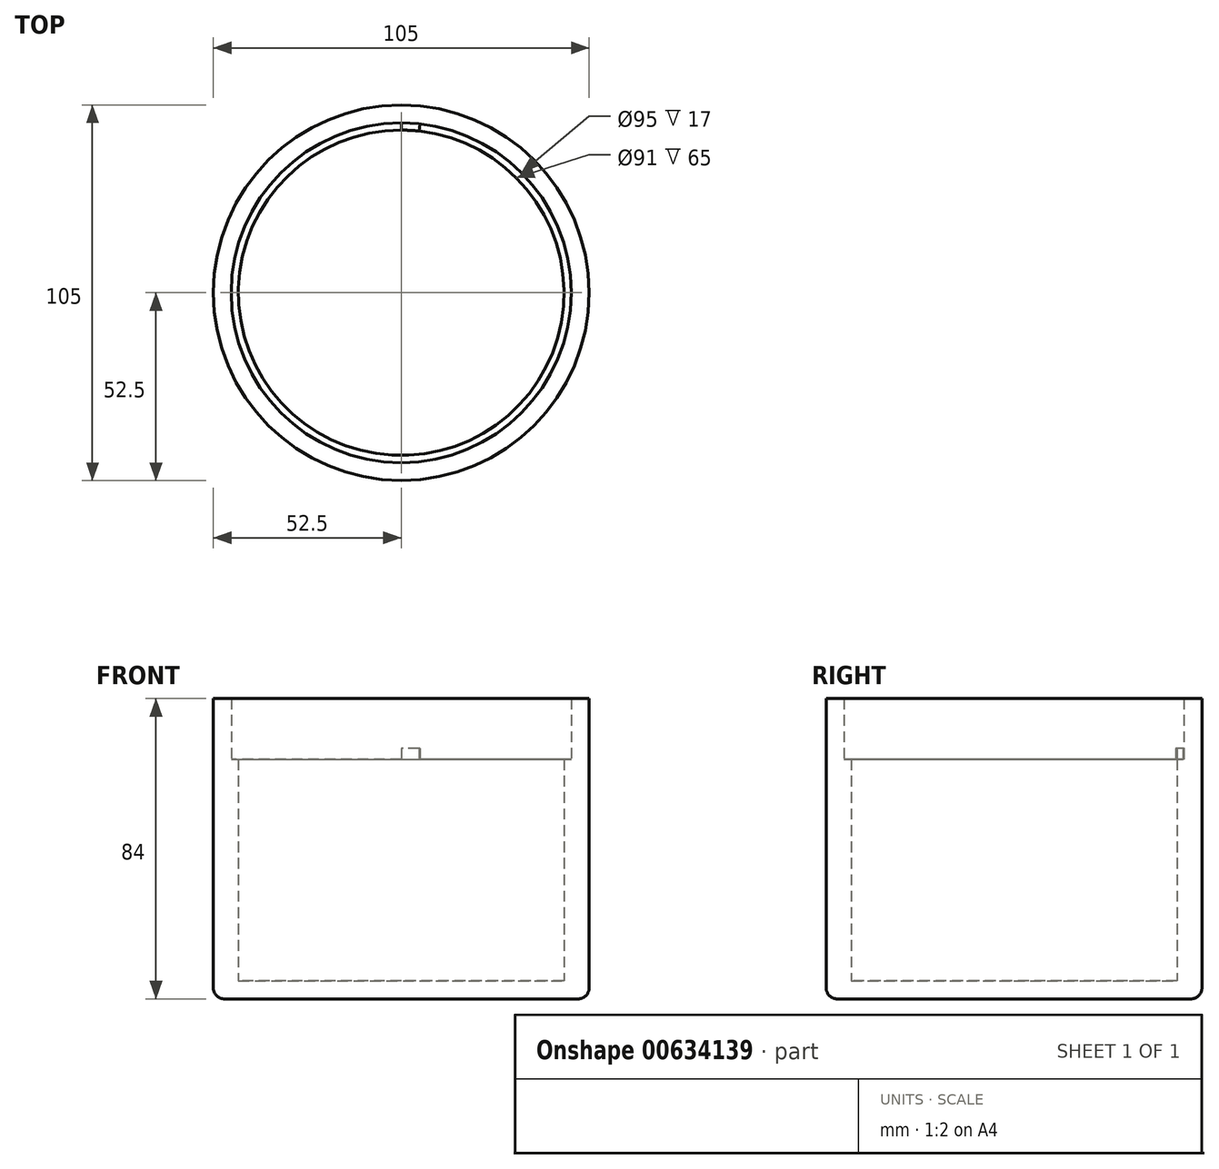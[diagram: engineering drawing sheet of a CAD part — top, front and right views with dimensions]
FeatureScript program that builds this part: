
annotation { "Feature Type Name" : "Feature", "Feature Type Description" : "" }
export const myFeature = defineFeature(function(context is Context, id is Id, definition is map)
    precondition{}
    {
        {
            var Q0;
            Q0=qCreatedBy(makeId("Top.planeOp"),FACE);
            var sketch = newSketch(context, id + "F0", { "sketchPlane" : qUnion([Q0])});
            skCircle(sketch, "E0", {"center": v(0, 0) * mm, "radius": 52.5 * mm});
            skSolve(sketch);
        }
        {
            var Q0;
            Q0=makeQuery(id+"F0.imprint","IMPRINT",FACE,{"disambiguationData":[TD([[makeQuery(id+"F0.imprint","IMPRINT",EDGE,{"derivedFrom":sQuery(id+"F0.wireOp",EDGE,"E0")}),1.0]])]});
            extrude(context, id + "F1", {"entities" : qUnion([Q0]), "depth" : 84 * mm, "offsetDistance" : 25 * mm});
        }
        {
            var Q0;
            Q0=makeQuery(id+"F1.opExtrude","CAP_FACE",FACE,{"disambiguationData":[OSD([sQuery(id+"F0.wireOp",EDGE,"E0")])],"isStart":false});
            shell(context, id + "F2", {"entities" : qUnion([Q0]), "thickness" : 5 * mm});
        }
        {
            var Q0;
            {var subQ0=sQuery(id+"F0.wireOp",EDGE,"E0");Q0=makeQuery(id+"F2.opShell","OFFSET_FACE",FACE,{"disambiguationData":[OSD([subQ0]),TDD([makeQuery(id+"F1.opExtrude","CAP_FACE",FACE,{"disambiguationData":[OSD([subQ0])],"isStart":true})])]});}
            var sketch = newSketch(context, id + "F3", { "sketchPlane" : qUnion([Q0])});
            skCircle(sketch, "E1", {"center": v(0, 0) * mm, "radius": 45.5 * mm});
            skSolve(sketch);
        }
        {
            var Q0;
            Q0=makeQuery(id+"F3.imprint","IMPRINT",FACE,{"disambiguationData":[TD([[makeQuery(id+"F3.imprint","IMPRINT",EDGE,{"derivedFrom":sQuery(id+"F3.wireOp",EDGE,"E1")}),-1.0]])]});
            extrude(context, id + "F4", {"entities" : qUnion([Q0]), "operationType" : NewBodyOperationType.ADD, "depth" : 62 * mm, "offsetDistance" : 25 * mm});
        }
        {
            var Q0;
            Q0=makeQuery(id+"F1.opExtrude","CAP_EDGE",EDGE,{"disambiguationData":[OSD([sQuery(id+"F0.wireOp",EDGE,"E0")])],"isStart":true});
            fillet(context, id + "F5", {"entities" : qUnion([Q0]), "radius" : 3 * mm, "tangentPropagation" : true, "allowEdgeOverflow" : false});
        }
        {
            var Q0;
            Q0=makeQuery(id+"F4.opExtrude","CAP_FACE",FACE,{"disambiguationData":[OSD([sQuery(id+"F0.wireOp",EDGE,"E0"),sQuery(id+"F3.wireOp",EDGE,"E1")])],"isStart":false});
            var sketch = newSketch(context, id + "F6", { "sketchPlane" : qUnion([Q0])});
            skLineSegment(sketch, "E2", {"start": v(0, 47.5) * mm, "end": v(0, 45.5) * mm});
            skLineSegment(sketch, "E3", {"start": v(5.2, 47.21) * mm, "end": v(4.99, 45.23) * mm});
            skArc(sketch, "E4", {"start": v(0, 45.5) * mm, "mid": v(2.5, 45.43) * mm, "end": v(4.99, 45.23) * mm});
            skArc(sketch, "E5", {"start": v(0, 47.5) * mm, "mid": v(2.6, 47.43) * mm, "end": v(5.2, 47.21) * mm});
            skArc(sketch, "E6", {"start": v(4.99, 45.23) * mm, "mid": v(9.92, 44.4) * mm, "end": v(14.73, 43.05) * mm});
            skArc(sketch, "E7", {"start": v(5.2, 47.21) * mm, "mid": v(10.36, 46.36) * mm, "end": v(15.38, 44.94) * mm});
            skLineSegment(sketch, "E8", {"start": v(14.73, 43.05) * mm, "end": v(15.38, 44.94) * mm});
            skSolve(sketch);
        }
        {
            var Q0;
            Q0=makeQuery(id+"F6.imprint","IMPRINT",FACE,{"disambiguationData":[TD([[makeQuery(id+"F6.imprint","IMPRINT",EDGE,{"derivedFrom":sQuery(id+"F6.wireOp",EDGE,"E2")}),1.0]])]});
            extrude(context, id + "F7", {"entities" : qUnion([Q0]), "operationType" : NewBodyOperationType.ADD, "depth" : 3 * mm, "offsetDistance" : 25 * mm});
        }
    });
